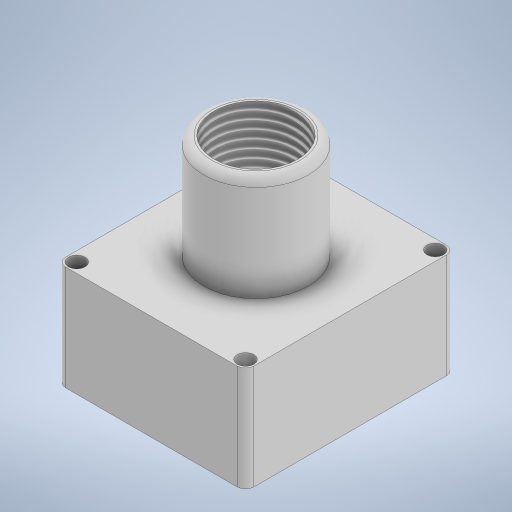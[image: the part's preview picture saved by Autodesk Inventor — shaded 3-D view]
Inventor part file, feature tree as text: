
AUTODESK INVENTOR PART (.ipt)
format: ipt  version: 2024 (Build 280153000, 153)  size: 271,872 bytes
history: native  units: mm
features: extrude x3, sketch x3, other x1, thread x1, fillet x1
ambient origin geometry x8: Origin, YZ Plane, XZ Plane, XY Plane, X Axis, Y Axis, Z Axis, Center Point
bodies: Body1 (feature_tree)
feature tree (9):
  other  "Sólido1"
  extrude  "Extrusión1"  Depth=100.0mm
  extrude  "Extrusión2"  Depth=4.0mm
  extrude  "Extrusión3"  Depth=4.0mm
  thread  "Rosca1"  [1 undecoded]
  fillet  "Empalme1"  Radius=5.0mm
  sketch  "Boceto1"  dims[d1=90.0mm d2=100.0mm]
  sketch  "Boceto2"  dims[d3=4.0mm d5=5.0mm]
  sketch  "Boceto3"  dims[d6=5.0mm d7=5.0mm d9=8.0mm d10=5.0mm d11=8.0mm d12=8.0mm d13=8.0mm d14=50.0mm d15=0.0mm d16=50.0mm d17=50.0mm d18=0.0mm d19=40.0mm d20=30.0mm d21=0.0mm d22=30.0mm d23=0.0mm d24=4.0mm]
note: 1 required parameter value undecoded (feature->parameter linkage not recoverable at this tier; creation-order binding heuristic only, values carry confidence <= 0.55)
